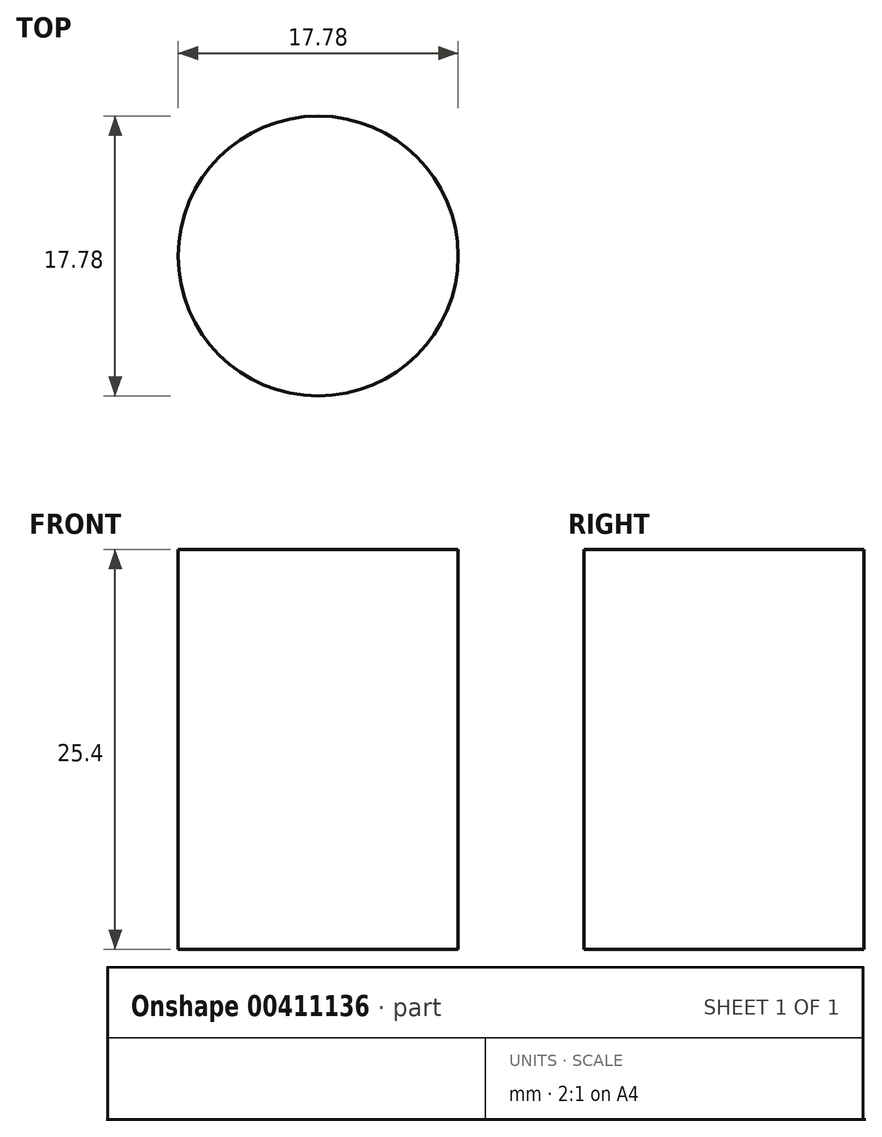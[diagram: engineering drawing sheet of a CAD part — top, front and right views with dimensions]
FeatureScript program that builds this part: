
annotation { "Feature Type Name" : "Feature", "Feature Type Description" : "" }
export const myFeature = defineFeature(function(context is Context, id is Id, definition is map)
    precondition{}
    {
        {
            var Q0;
            Q0=qCreatedBy(makeId("Top.planeOp"),FACE);
            var sketch = newSketch(context, id + "F0", { "sketchPlane" : qUnion([Q0])});
            skCircle(sketch, "E0", {"center": v(0, 0) * mm, "radius": 8.9 * mm});
            skSolve(sketch);
        }
        {
            var Q0;
            Q0=makeQuery(id+"F0.imprint","IMPRINT",FACE,{"disambiguationData":[TD([[makeQuery(id+"F0.imprint","IMPRINT",EDGE,{"derivedFrom":sQuery(id+"F0.wireOp",EDGE,"E0")}),1.0]])]});
            extrude(context, id + "F1", {"entities" : qUnion([Q0]), "depth" : 25.4 * mm});
        }
    });
